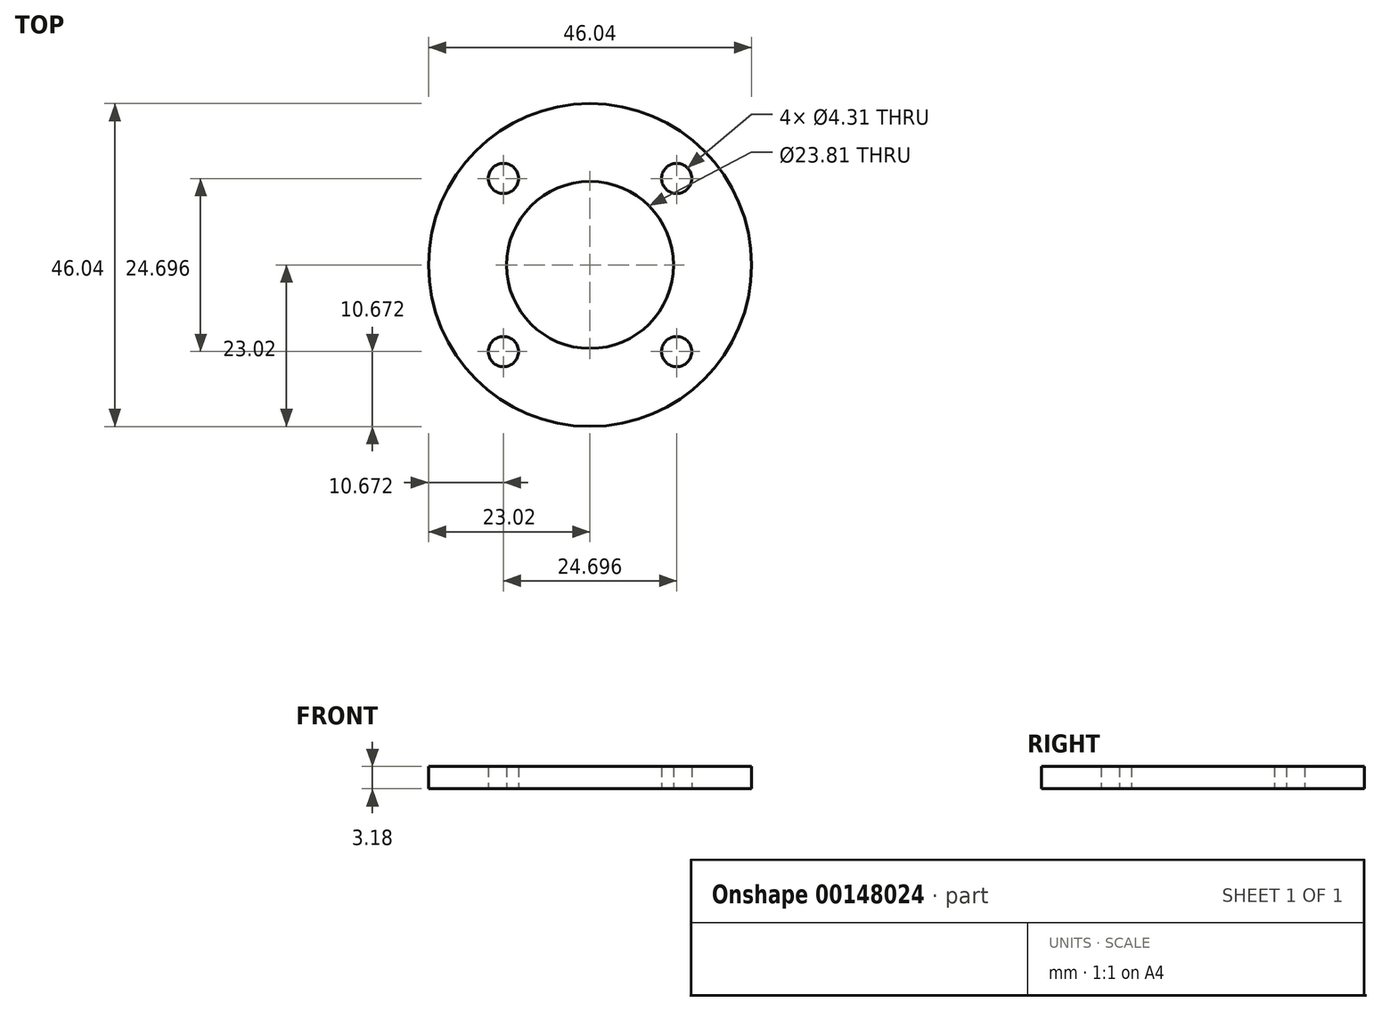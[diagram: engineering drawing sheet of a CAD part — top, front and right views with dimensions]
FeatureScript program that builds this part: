
annotation { "Feature Type Name" : "Feature", "Feature Type Description" : "" }
export const myFeature = defineFeature(function(context is Context, id is Id, definition is map)
    precondition{}
    {
        {
            var Q0;
            Q0=qCreatedBy(makeId("Top.planeOp"),FACE);
            var sketch = newSketch(context, id + "F0", { "sketchPlane" : qUnion([Q0])});
            skCircle(sketch, "E0", {"center": v(0, 0) * mm, "radius": 23.02 * mm});
            skCircle(sketch, "E1", {"center": v(0, 0) * mm, "radius": 11.9 * mm});
            skLineSegment(sketch, "E2.bottom", {"start": v(-12.35, 12.35) * mm, "end": v(12.35, 12.35) * mm, "construction": true});
            skLineSegment(sketch, "E2.top", {"start": v(-12.35, -12.35) * mm, "end": v(12.35, -12.35) * mm, "construction": true});
            skLineSegment(sketch, "E2.left", {"start": v(-12.35, 12.35) * mm, "end": v(-12.35, -12.35) * mm, "construction": true});
            skLineSegment(sketch, "E2.right", {"start": v(12.35, 12.35) * mm, "end": v(12.35, -12.35) * mm, "construction": true});
            skCircle(sketch, "E3", {"center": v(-12.35, 12.35) * mm, "radius": 5.56 * mm, "construction": true});
            skCircle(sketch, "E4", {"center": v(12.35, 12.35) * mm, "radius": 2.15 * mm});
            skCircle(sketch, "E5", {"center": v(-12.35, 12.35) * mm, "radius": 2.15 * mm});
            skCircle(sketch, "E6", {"center": v(-12.35, -12.35) * mm, "radius": 2.15 * mm});
            skCircle(sketch, "E7", {"center": v(12.35, -12.35) * mm, "radius": 2.15 * mm});
            skSolve(sketch);
        }
        {
            var Q0;
            Q0=qSketchRegion(id+"F0",true);
            extrude(context, id + "F1", {"entities" : qUnion([Q0]), "depth" : 3.17 * mm});
        }
    });
